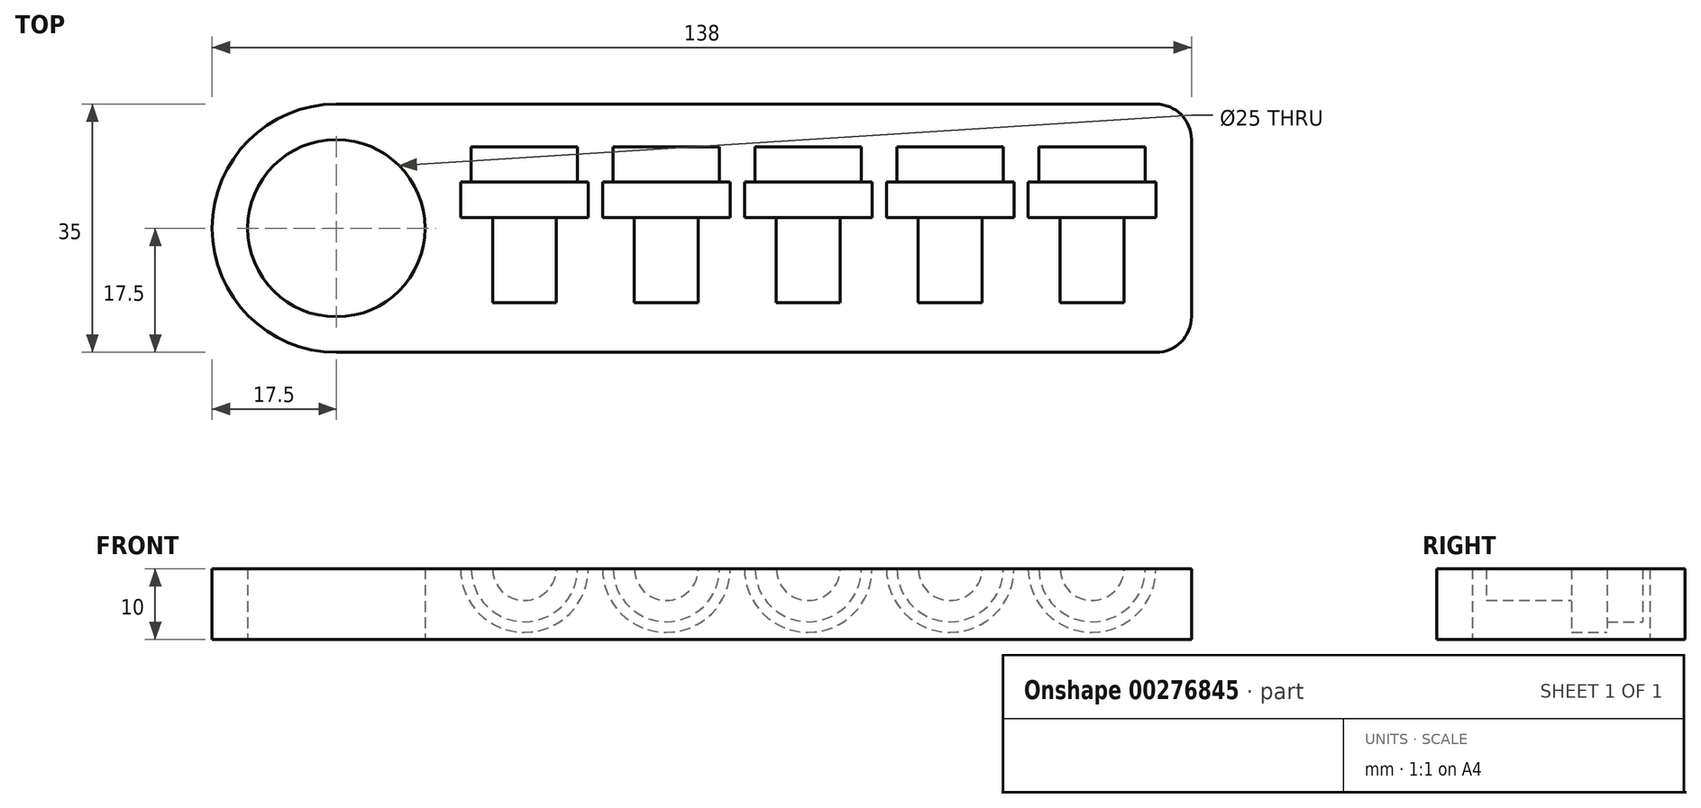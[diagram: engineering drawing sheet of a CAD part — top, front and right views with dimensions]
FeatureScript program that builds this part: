
annotation { "Feature Type Name" : "Feature", "Feature Type Description" : "" }
export const myFeature = defineFeature(function(context is Context, id is Id, definition is map)
    precondition{}
    {
        {
            var Q0;
            Q0=qCreatedBy(makeId("Top.planeOp"),FACE);
            var sketch = newSketch(context, id + "F0", { "sketchPlane" : qUnion([Q0])});
            skLineSegment(sketch, "E0.bottom", {"start": v(17.5, 0) * mm, "end": v(133, 0) * mm});
            skLineSegment(sketch, "E0.top", {"start": v(17.5, 35) * mm, "end": v(133, 35) * mm});
            skLineSegment(sketch, "E0.left", {"start": v(0, 17.5) * mm, "end": v(0, 17.5) * mm});
            skLineSegment(sketch, "E0.right", {"start": v(138, 5) * mm, "end": v(138, 30) * mm});
            skLineSegment(sketch, "E1.bottom", {"start": v(0, 0) * mm, "end": v(17.5, 0) * mm, "construction": true});
            skLineSegment(sketch, "E1.top", {"start": v(0, 17.5) * mm, "end": v(17.5, 17.5) * mm, "construction": true});
            skLineSegment(sketch, "E1.left", {"start": v(0, 0) * mm, "end": v(0, 17.5) * mm, "construction": true});
            skLineSegment(sketch, "E1.right", {"start": v(17.5, 0) * mm, "end": v(17.5, 17.5) * mm, "construction": true});
            skCircle(sketch, "E2", {"center": v(17.5, 17.5) * mm, "radius": 12.5 * mm});
            skPoint(sketch, "E3.visualSharp", {"position": v(0, 0) * mm});
            skArc(sketch, "E3.filletArc", {"start": v(0, 17.5) * mm, "mid": v(5.13, 5.13) * mm, "end": v(17.5, 0) * mm});
            skPoint(sketch, "E4.visualSharp", {"position": v(0, 35) * mm});
            skArc(sketch, "E4.filletArc", {"start": v(17.5, 35) * mm, "mid": v(5.13, 29.87) * mm, "end": v(0, 17.5) * mm});
            skPoint(sketch, "E5.visualSharp", {"position": v(138, 35) * mm});
            skArc(sketch, "E5.filletArc", {"start": v(138, 30) * mm, "mid": v(136.54, 33.54) * mm, "end": v(133, 35) * mm});
            skPoint(sketch, "E6.visualSharp", {"position": v(138, 0) * mm});
            skArc(sketch, "E6.filletArc", {"start": v(133, 0) * mm, "mid": v(136.54, 1.46) * mm, "end": v(138, 5) * mm});
            skSolve(sketch);
        }
        {
            var Q0;
            Q0=makeQuery(id+"F0.imprint","IMPRINT",FACE,{"disambiguationData":[TD([[makeQuery(id+"F0.imprint","IMPRINT",EDGE,{"derivedFrom":sQuery(id+"F0.wireOp",EDGE,"E0.bottom")}),1.0]])]});
            extrude(context, id + "F1", {"entities" : qUnion([Q0]), "depth" : 10 * mm});
        }
        {
            var Q0;
            Q0=makeQuery(id+"F1.opExtrude","CAP_FACE",FACE,{"disambiguationData":[OSD([sQuery(id+"F0.wireOp",EDGE,"E0.bottom"),sQuery(id+"F0.wireOp",EDGE,"E0.top"),sQuery(id+"F0.wireOp",EDGE,"E0.right"),sQuery(id+"F0.wireOp",EDGE,"E2"),sQuery(id+"F0.wireOp",EDGE,"E3.filletArc"),sQuery(id+"F0.wireOp",EDGE,"E4.filletArc"),sQuery(id+"F0.wireOp",EDGE,"E5.filletArc"),sQuery(id+"F0.wireOp",EDGE,"E6.filletArc")])],"isStart":false});
            var sketch = newSketch(context, id + "F2", { "sketchPlane" : qUnion([Q0])});
            skLineSegment(sketch, "E7.bottom", {"start": v(0, 0) * mm, "end": v(44, 0) * mm, "construction": true});
            skLineSegment(sketch, "E7.top", {"start": v(0, 7) * mm, "end": v(44, 7) * mm, "construction": true});
            skLineSegment(sketch, "E7.left", {"start": v(0, 0) * mm, "end": v(0, 7) * mm, "construction": true});
            skLineSegment(sketch, "E7.right", {"start": v(44, 0) * mm, "end": v(44, 7) * mm, "construction": true});
            skLineSegment(sketch, "E8.bottom", {"start": v(44, 7) * mm, "end": v(48.5, 7) * mm});
            skLineSegment(sketch, "E8.left", {"start": v(44, 7) * mm, "end": v(44, 19) * mm});
            skLineSegment(sketch, "E8.right", {"start": v(48.5, 7) * mm, "end": v(48.5, 19) * mm});
            skLineSegment(sketch, "E9", {"start": v(44, 7) * mm, "end": v(64, 7) * mm, "construction": true});
            skPoint(sketch, "E9.endSnap0", {"position": v(46.25, 7) * mm});
            skLineSegment(sketch, "E10", {"start": v(64, 7) * mm, "end": v(84, 7) * mm, "construction": true});
            skLineSegment(sketch, "E11", {"start": v(84, 7) * mm, "end": v(104, 7) * mm, "construction": true});
            skLineSegment(sketch, "E12", {"start": v(104, 7) * mm, "end": v(124, 7) * mm, "construction": true});
            skLineSegment(sketch, "E13.bottom", {"start": v(64, 7) * mm, "end": v(68.5, 7) * mm});
            skLineSegment(sketch, "E13.left", {"start": v(64, 7) * mm, "end": v(64, 19) * mm});
            skLineSegment(sketch, "E13.right", {"start": v(68.5, 7) * mm, "end": v(68.5, 19) * mm});
            skLineSegment(sketch, "E14.bottom", {"start": v(84, 7) * mm, "end": v(88.5, 7) * mm});
            skLineSegment(sketch, "E14.left", {"start": v(84, 7) * mm, "end": v(84, 19) * mm});
            skLineSegment(sketch, "E14.right", {"start": v(88.5, 7) * mm, "end": v(88.5, 19) * mm});
            skLineSegment(sketch, "E15.bottom", {"start": v(104, 7) * mm, "end": v(108.5, 7) * mm});
            skLineSegment(sketch, "E15.left", {"start": v(104, 7) * mm, "end": v(104, 19) * mm});
            skLineSegment(sketch, "E15.right", {"start": v(108.5, 7) * mm, "end": v(108.5, 19) * mm});
            skLineSegment(sketch, "E16.bottom", {"start": v(124, 7) * mm, "end": v(128.5, 7) * mm});
            skLineSegment(sketch, "E16.left", {"start": v(124, 7) * mm, "end": v(124, 19) * mm});
            skLineSegment(sketch, "E16.right", {"start": v(128.5, 7) * mm, "end": v(128.5, 19) * mm});
            skLineSegment(sketch, "E17.bottom", {"start": v(128.5, 19) * mm, "end": v(133, 19) * mm});
            skLineSegment(sketch, "E17.top", {"start": v(131.5, 24) * mm, "end": v(133, 24) * mm});
            skLineSegment(sketch, "E17.left", {"start": v(124, 19) * mm, "end": v(124, 24) * mm});
            skLineSegment(sketch, "E17.right", {"start": v(133, 19) * mm, "end": v(133, 24) * mm});
            skLineSegment(sketch, "E18.bottom", {"start": v(108.5, 19) * mm, "end": v(113, 19) * mm});
            skLineSegment(sketch, "E18.top", {"start": v(111.5, 24) * mm, "end": v(113, 24) * mm});
            skLineSegment(sketch, "E18.left", {"start": v(104, 19) * mm, "end": v(104, 24) * mm});
            skLineSegment(sketch, "E18.right", {"start": v(113, 19) * mm, "end": v(113, 24) * mm});
            skLineSegment(sketch, "E19.bottom", {"start": v(88.5, 19) * mm, "end": v(93, 19) * mm});
            skLineSegment(sketch, "E19.top", {"start": v(91.5, 24) * mm, "end": v(93, 24) * mm});
            skLineSegment(sketch, "E19.left", {"start": v(84, 19) * mm, "end": v(84, 24) * mm});
            skLineSegment(sketch, "E19.right", {"start": v(93, 19) * mm, "end": v(93, 24) * mm});
            skLineSegment(sketch, "E20.bottom", {"start": v(68.5, 19) * mm, "end": v(73, 19) * mm});
            skLineSegment(sketch, "E20.top", {"start": v(71.5, 24) * mm, "end": v(73, 24) * mm});
            skLineSegment(sketch, "E20.left", {"start": v(64, 19) * mm, "end": v(64, 24) * mm});
            skLineSegment(sketch, "E20.right", {"start": v(73, 19) * mm, "end": v(73, 24) * mm});
            skLineSegment(sketch, "E21.bottom", {"start": v(48.5, 19) * mm, "end": v(53, 19) * mm});
            skLineSegment(sketch, "E21.top", {"start": v(51.5, 24) * mm, "end": v(53, 24) * mm});
            skLineSegment(sketch, "E21.left", {"start": v(44, 19) * mm, "end": v(44, 24) * mm});
            skLineSegment(sketch, "E21.right", {"start": v(53, 19) * mm, "end": v(53, 24) * mm});
            skLineSegment(sketch, "E22.top", {"start": v(124, 29) * mm, "end": v(131.5, 29) * mm});
            skLineSegment(sketch, "E22.left", {"start": v(124, 24) * mm, "end": v(124, 29) * mm});
            skLineSegment(sketch, "E22.right", {"start": v(131.5, 24) * mm, "end": v(131.5, 29) * mm});
            skLineSegment(sketch, "E23.top", {"start": v(104, 29) * mm, "end": v(111.5, 29) * mm});
            skLineSegment(sketch, "E23.left", {"start": v(104, 24) * mm, "end": v(104, 29) * mm});
            skLineSegment(sketch, "E23.right", {"start": v(111.5, 24) * mm, "end": v(111.5, 29) * mm});
            skLineSegment(sketch, "E24.top", {"start": v(84, 29) * mm, "end": v(91.5, 29) * mm});
            skLineSegment(sketch, "E24.left", {"start": v(84, 24) * mm, "end": v(84, 29) * mm});
            skLineSegment(sketch, "E24.right", {"start": v(91.5, 24) * mm, "end": v(91.5, 29) * mm});
            skLineSegment(sketch, "E25.top", {"start": v(64, 29) * mm, "end": v(71.5, 29) * mm});
            skLineSegment(sketch, "E25.left", {"start": v(64, 24) * mm, "end": v(64, 29) * mm});
            skLineSegment(sketch, "E25.right", {"start": v(71.5, 24) * mm, "end": v(71.5, 29) * mm});
            skLineSegment(sketch, "E26.top", {"start": v(44, 29) * mm, "end": v(51.5, 29) * mm});
            skLineSegment(sketch, "E26.left", {"start": v(44, 24) * mm, "end": v(44, 29) * mm});
            skLineSegment(sketch, "E26.right", {"start": v(51.5, 24) * mm, "end": v(51.5, 29) * mm});
            skSolve(sketch);
        }
        {
            var Q0;
            Q0=makeQuery(id+"F2.imprint","IMPRINT",FACE,{"disambiguationData":[TD([[makeQuery(id+"F2.imprint","IMPRINT",EDGE,{"derivedFrom":sQuery(id+"F2.wireOp",EDGE,"E8.bottom")}),1.0]])]});
            var Q1;
            Q1=sQuery(id+"F2.wireOp",EDGE,"E8.left");
            revolve(context, id + "F3", {"operationType" : NewBodyOperationType.REMOVE, "entities" : qUnion([Q0]), "axis" : qUnion([Q1]), "revolveType" : RevolveType.FULL, "oppositeDirection" : true});
        }
        {
            var Q0;
            Q0=makeQuery(id+"F2.imprint","IMPRINT",FACE,{"disambiguationData":[TD([[makeQuery(id+"F2.imprint","IMPRINT",EDGE,{"derivedFrom":sQuery(id+"F2.wireOp",EDGE,"E13.bottom")}),1.0]])]});
            var Q1;
            Q1=sQuery(id+"F2.wireOp",EDGE,"E20.left");
            revolve(context, id + "F4", {"operationType" : NewBodyOperationType.REMOVE, "entities" : qUnion([Q0]), "axis" : qUnion([Q1]), "revolveType" : RevolveType.FULL, "oppositeDirection" : true});
        }
        {
            var Q0;
            Q0=makeQuery(id+"F2.imprint","IMPRINT",FACE,{"disambiguationData":[TD([[makeQuery(id+"F2.imprint","IMPRINT",EDGE,{"derivedFrom":sQuery(id+"F2.wireOp",EDGE,"E14.bottom")}),1.0]])]});
            var Q1;
            Q1=sQuery(id+"F2.wireOp",EDGE,"E19.left");
            revolve(context, id + "F5", {"operationType" : NewBodyOperationType.REMOVE, "entities" : qUnion([Q0]), "axis" : qUnion([Q1]), "revolveType" : RevolveType.FULL, "oppositeDirection" : true});
        }
        {
            var Q0;
            Q0=makeQuery(id+"F2.imprint","IMPRINT",FACE,{"disambiguationData":[TD([[makeQuery(id+"F2.imprint","IMPRINT",EDGE,{"derivedFrom":sQuery(id+"F2.wireOp",EDGE,"E15.bottom")}),1.0]])]});
            var Q1;
            Q1=sQuery(id+"F2.wireOp",EDGE,"E15.left");
            revolve(context, id + "F6", {"operationType" : NewBodyOperationType.REMOVE, "entities" : qUnion([Q0]), "axis" : qUnion([Q1]), "revolveType" : RevolveType.FULL, "oppositeDirection" : true});
        }
        {
            var Q0;
            Q0=makeQuery(id+"F2.imprint","IMPRINT",FACE,{"disambiguationData":[TD([[makeQuery(id+"F2.imprint","IMPRINT",EDGE,{"derivedFrom":sQuery(id+"F2.wireOp",EDGE,"E16.bottom")}),1.0]])]});
            var Q1;
            Q1=sQuery(id+"F2.wireOp",EDGE,"E16.left");
            revolve(context, id + "F7", {"operationType" : NewBodyOperationType.REMOVE, "entities" : qUnion([Q0]), "axis" : qUnion([Q1]), "revolveType" : RevolveType.FULL, "oppositeDirection" : true});
        }
    });
